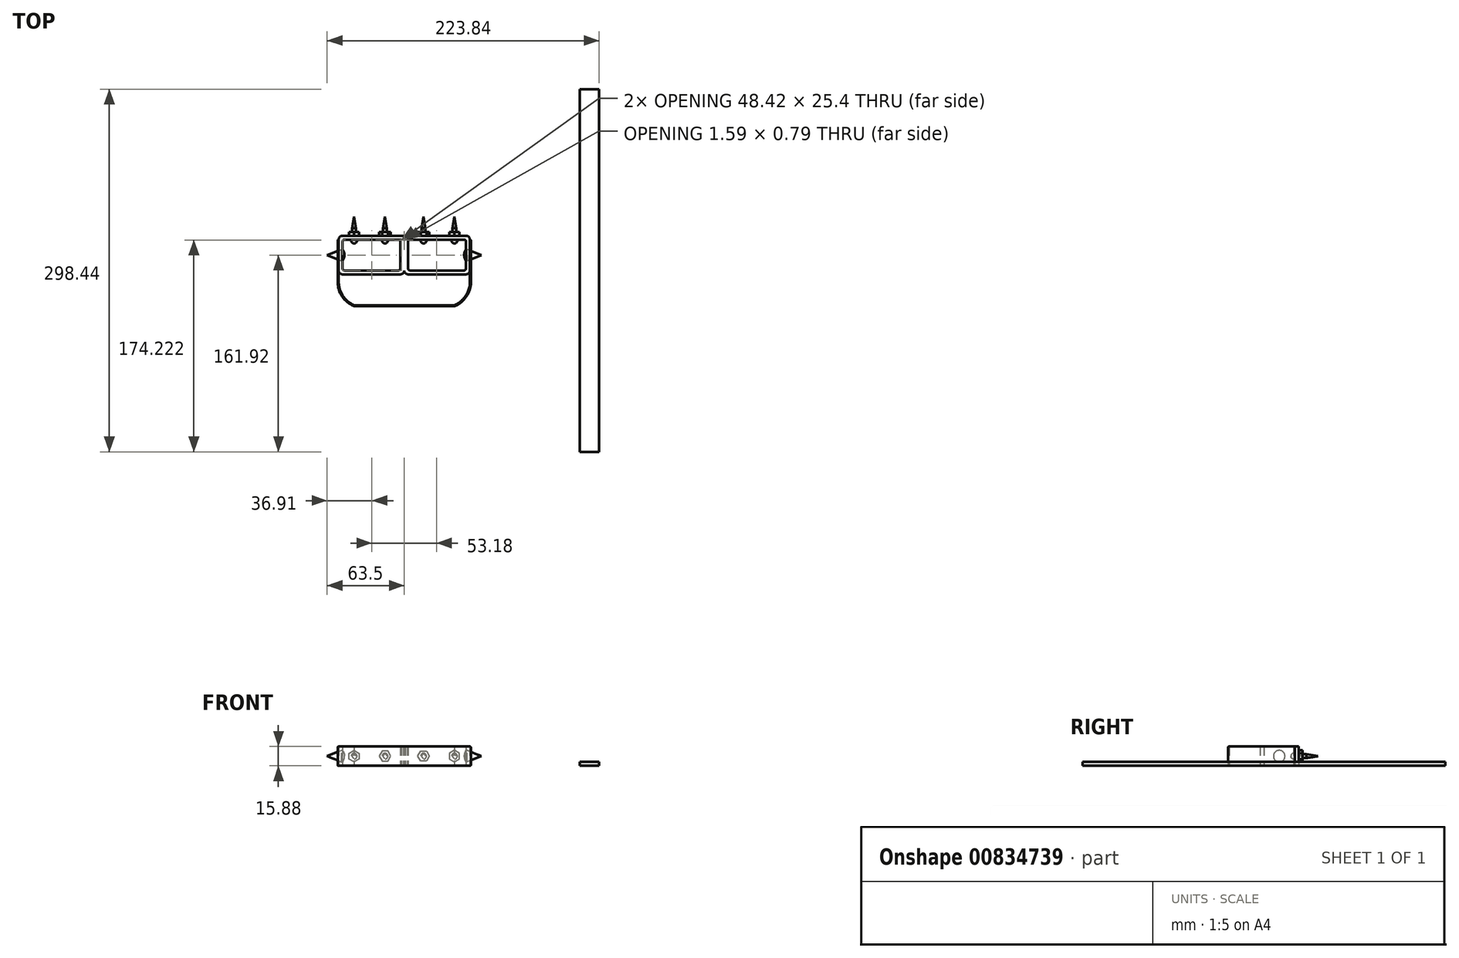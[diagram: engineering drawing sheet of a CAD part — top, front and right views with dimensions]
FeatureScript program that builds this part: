
annotation { "Feature Type Name" : "Feature", "Feature Type Description" : "" }
export const myFeature = defineFeature(function(context is Context, id is Id, definition is map)
    precondition{}
    {
        {
            var Q0;
            Q0=qCreatedBy(makeId("Top.planeOp"),FACE);
            var sketch = newSketch(context, id + "F0", { "sketchPlane" : qUnion([Q0])});
            skLineSegment(sketch, "E0.bottom", {"start": v(-49.21, 0) * mm, "end": v(-4.76, 0) * mm});
            skLineSegment(sketch, "E0.top", {"start": v(-49.21, 25.4) * mm, "end": v(49.21, 25.4) * mm});
            skLineSegment(sketch, "E0.left", {"start": v(-50.8, 1.59) * mm, "end": v(-50.8, 23.81) * mm});
            skLineSegment(sketch, "E0.right", {"start": v(50.8, 1.59) * mm, "end": v(50.8, 23.81) * mm});
            skLineSegment(sketch, "E1", {"start": v(0, 0) * mm, "end": v(0, 24.6) * mm});
            skLineSegment(sketch, "E2", {"start": v(-3.18, 24.6) * mm, "end": v(-3.18, 1.59) * mm});
            skLineSegment(sketch, "E3", {"start": v(3.17, 24.6) * mm, "end": v(3.17, 1.59) * mm});
            skLineSegment(sketch, "E4.bottom", {"start": v(3.18, -3.18) * mm, "end": v(50.8, -3.18) * mm});
            skLineSegment(sketch, "E4.top", {"start": v(-50.8, 28.57) * mm, "end": v(50.8, 28.57) * mm});
            skLineSegment(sketch, "E4.left", {"start": v(-53.98, 0) * mm, "end": v(-53.98, 25.4) * mm});
            skLineSegment(sketch, "E4.right", {"start": v(53.97, 0) * mm, "end": v(53.97, 25.4) * mm});
            skLineSegment(sketch, "E5", {"start": v(0, 0) * mm, "end": v(0, 0) * mm});
            skLineSegment(sketch, "E6.trimOffspring", {"start": v(4.76, 0) * mm, "end": v(49.21, 0) * mm});
            skPoint(sketch, "E7.visualSharp", {"position": v(-50.8, 25.4) * mm});
            skArc(sketch, "E7.filletArc", {"start": v(-49.21, 25.4) * mm, "mid": v(-50.34, 24.94) * mm, "end": v(-50.8, 23.81) * mm});
            skPoint(sketch, "E8.visualSharp", {"position": v(-53.98, 28.57) * mm});
            skArc(sketch, "E8.filletArc", {"start": v(-50.8, 28.57) * mm, "mid": v(-53.05, 27.65) * mm, "end": v(-53.98, 25.4) * mm});
            skPoint(sketch, "E9.visualSharp", {"position": v(-50.8, 0) * mm});
            skArc(sketch, "E9.filletArc", {"start": v(-50.8, 1.59) * mm, "mid": v(-50.34, 0.46) * mm, "end": v(-49.21, 0) * mm});
            skPoint(sketch, "E10.visualSharp", {"position": v(-3.17, 0) * mm});
            skArc(sketch, "E10.filletArc", {"start": v(-4.76, 0) * mm, "mid": v(-3.64, 0.46) * mm, "end": v(-3.18, 1.59) * mm});
            skPoint(sketch, "E11.visualSharp", {"position": v(3.17, 0) * mm});
            skArc(sketch, "E11.filletArc", {"start": v(3.17, 1.59) * mm, "mid": v(3.64, 0.46) * mm, "end": v(4.76, 0) * mm});
            skPoint(sketch, "E12.visualSharp", {"position": v(50.8, 0) * mm});
            skArc(sketch, "E12.filletArc", {"start": v(49.21, 0) * mm, "mid": v(50.34, 0.46) * mm, "end": v(50.8, 1.59) * mm});
            skPoint(sketch, "E13.visualSharp", {"position": v(50.8, 25.4) * mm});
            skArc(sketch, "E13.filletArc", {"start": v(50.8, 23.81) * mm, "mid": v(50.34, 24.94) * mm, "end": v(49.21, 25.4) * mm});
            skPoint(sketch, "E14.visualSharp", {"position": v(53.97, 28.57) * mm});
            skArc(sketch, "E14.filletArc", {"start": v(53.97, 25.4) * mm, "mid": v(53.05, 27.65) * mm, "end": v(50.8, 28.58) * mm});
            skPoint(sketch, "E15.visualSharp", {"position": v(53.97, -3.18) * mm});
            skArc(sketch, "E15.filletArc", {"start": v(50.8, -3.18) * mm, "mid": v(53.05, -2.25) * mm, "end": v(53.97, 0) * mm});
            skPoint(sketch, "E16.newPointB", {"position": v(0, -3.18) * mm});
            skArc(sketch, "E16.filletArc", {"start": v(0, 0) * mm, "mid": v(0.93, -2.25) * mm, "end": v(3.18, -3.17) * mm});
            skLineSegment(sketch, "E17", {"start": v(0, -3.18) * mm, "end": v(0, -3.18) * mm});
            skLineSegment(sketch, "E18", {"start": v(-3.18, -3.18) * mm, "end": v(-50.8, -3.18) * mm});
            skArc(sketch, "E19.filletArc", {"start": v(-3.18, -3.17) * mm, "mid": v(-0.93, -2.25) * mm, "end": v(0, 0) * mm});
            skPoint(sketch, "E20.visualSharp", {"position": v(-53.98, -3.18) * mm});
            skArc(sketch, "E20.filletArc", {"start": v(-53.97, 0) * mm, "mid": v(-53.05, -2.25) * mm, "end": v(-50.8, -3.18) * mm});
            skLineSegment(sketch, "E21", {"start": v(-2.38, 25.4) * mm, "end": v(-0.8, 25.4) * mm});
            skLineSegment(sketch, "E22", {"start": v(0.8, 25.4) * mm, "end": v(2.38, 25.4) * mm});
            skPoint(sketch, "E23.visualSharp", {"position": v(3.17, 25.4) * mm});
            skArc(sketch, "E23.filletArc", {"start": v(3.17, 24.6) * mm, "mid": v(2.94, 25.17) * mm, "end": v(2.38, 25.4) * mm});
            skPoint(sketch, "E24.visualSharp", {"position": v(0, 25.4) * mm});
            skArc(sketch, "E24.filletArc", {"start": v(0.8, 25.4) * mm, "mid": v(0.23, 25.17) * mm, "end": v(0, 24.6) * mm});
            skLineSegment(sketch, "E25", {"start": v(0, 24.6) * mm, "end": v(0, 24.6) * mm});
            skArc(sketch, "E26.filletArc", {"start": v(0, 24.6) * mm, "mid": v(-0.23, 25.17) * mm, "end": v(-0.8, 25.4) * mm});
            skPoint(sketch, "E27.visualSharp", {"position": v(-3.18, 25.4) * mm});
            skArc(sketch, "E27.filletArc", {"start": v(-2.38, 25.4) * mm, "mid": v(-2.94, 25.17) * mm, "end": v(-3.18, 24.6) * mm});
            skLineSegment(sketch, "E28.bottom", {"start": v(-53.97, -3.18) * mm, "end": v(53.97, -3.18) * mm, "construction": true});
            skLineSegment(sketch, "E28.top", {"start": v(-41.27, -28.58) * mm, "end": v(41.28, -28.58) * mm});
            skLineSegment(sketch, "E28.left", {"start": v(-53.98, -3.18) * mm, "end": v(-53.98, -9.53) * mm});
            skLineSegment(sketch, "E28.right", {"start": v(53.97, -3.18) * mm, "end": v(53.97, -9.53) * mm});
            skLineSegment(sketch, "E29", {"start": v(-53.98, 0) * mm, "end": v(-53.98, -3.18) * mm});
            skLineSegment(sketch, "E30", {"start": v(53.97, 0) * mm, "end": v(53.97, -3.18) * mm});
            skPoint(sketch, "E31", {"position": v(-53.97, -9.53) * mm});
            skPoint(sketch, "E32", {"position": v(-41.27, -28.58) * mm});
            skPoint(sketch, "E33", {"position": v(41.28, -28.58) * mm});
            skPoint(sketch, "E34", {"position": v(53.98, -9.53) * mm});
            skArc(sketch, "E35", {"start": v(-53.97, -9.53) * mm, "mid": v(-50.5, -20.97) * mm, "end": v(-41.27, -28.58) * mm});
            skArc(sketch, "E36", {"start": v(41.28, -28.58) * mm, "mid": v(50.5, -20.97) * mm, "end": v(53.98, -9.53) * mm});
            skPoint(sketch, "E37.orphan", {"position": v(53.97, -28.58) * mm});
            skPoint(sketch, "E38.orphan", {"position": v(-53.97, -28.58) * mm});
            skLineSegment(sketch, "E39", {"start": v(54.77, 25.4) * mm, "end": v(54.77, -9.53) * mm});
            skLineSegment(sketch, "E40", {"start": v(-54.77, 25.4) * mm, "end": v(-54.77, -9.53) * mm});
            skLineSegment(sketch, "E41", {"start": v(-41.27, -29.37) * mm, "end": v(41.27, -29.37) * mm});
            skLineSegment(sketch, "E42", {"start": v(-54.77, 25.4) * mm, "end": v(-53.98, 25.4) * mm});
            skLineSegment(sketch, "E43", {"start": v(54.77, 25.4) * mm, "end": v(53.97, 25.4) * mm});
            skArc(sketch, "E44", {"start": v(41.27, -29.37) * mm, "mid": v(51.08, -21.52) * mm, "end": v(54.77, -9.53) * mm});
            skArc(sketch, "E45", {"start": v(-54.77, -9.53) * mm, "mid": v(-51.08, -21.52) * mm, "end": v(-41.27, -29.37) * mm});
            skSolve(sketch);
        }
        {
            var Q0;
            Q0=makeQuery(id+"F0.imprint","IMPRINT",FACE,{"disambiguationData":[TD([[makeQuery(id+"F0.imprint","IMPRINT",EDGE,{"derivedFrom":sQuery(id+"F0.wireOp",EDGE,"E0.bottom")}),-1.0]])]});
            extrude(context, id + "F1", {"entities" : qUnion([Q0]), "depth" : 15.88 * mm, "offsetDistance" : 25.4 * mm});
        }
        {
            var Q0;
            Q0=sQuery(id+"F0.wireOp",EDGE,"E1");
            extrude(context, id + "F2", {"bodyType" : ToolBodyType.SURFACE, "surfaceEntities" : qUnion([Q0]), "depth" : 15.88 * mm, "offsetDistance" : 25.4 * mm});
        }
        {
            var Q0;
            Q0=sQuery(id+"F0.wireOp",EDGE,"E22");
            var Q1;
            Q1=sQuery(id+"F0.wireOp",EDGE,"E21");
            extrude(context, id + "F3", {"bodyType" : ToolBodyType.SURFACE, "surfaceEntities" : qUnion([Q0, Q1]), "depth" : 15.88 * mm, "offsetDistance" : 25.4 * mm});
        }
        {
            var Q0;
            Q0=makeQuery(id+"F0.imprint","IMPRINT",FACE,{"disambiguationData":[TD([[makeQuery(id+"F0.imprint","IMPRINT",EDGE,{"derivedFrom":sQuery(id+"F0.wireOp",EDGE,"E4.bottom")}),-1.0]])]});
            extrude(context, id + "F4", {"entities" : qUnion([Q0]), "depth" : 15.88 * mm, "offsetDistance" : 25.4 * mm});
        }
        {
            var Q0;
            Q0=makeQuery(id+"F0.imprint","IMPRINT",FACE,{"disambiguationData":[TD([[makeQuery(id+"F0.imprint","IMPRINT",EDGE,{"derivedFrom":sQuery(id+"F0.wireOp",EDGE,"E4.left")}),1.0]])]});
            extrude(context, id + "F5", {"entities" : qUnion([Q0]), "depth" : 15.88 * mm, "offsetDistance" : 25.4 * mm});
        }
        {
            var Q0;
            Q0=makeQuery(id+"F5.opExtrude","SWEPT_FACE",FACE,{"disambiguationData":[OSD([sQuery(id+"F0.wireOp",EDGE,"E41")])]});
            var Q1;
            Q1=makeQuery(id+"F5.opExtrude","SWEPT_FACE",FACE,{"disambiguationData":[OSD([sQuery(id+"F0.wireOp",EDGE,"E45")])]});
            var Q2;
            Q2=makeQuery(id+"F5.opExtrude","SWEPT_FACE",FACE,{"disambiguationData":[OSD([sQuery(id+"F0.wireOp",EDGE,"E40")])]});
            var Q3;
            Q3=makeQuery(id+"F5.opExtrude","SWEPT_FACE",FACE,{"disambiguationData":[OSD([sQuery(id+"F0.wireOp",EDGE,"E44")])]});
            var Q4;
            Q4=makeQuery(id+"F5.opExtrude","SWEPT_FACE",FACE,{"disambiguationData":[OSD([sQuery(id+"F0.wireOp",EDGE,"E39")])]});
            fillet(context, id + "F6", {"entities" : qUnion([Q0, Q1, Q2, Q3, Q4]), "radius" : 0.8 * mm, "tangentPropagation" : true, "allowEdgeOverflow" : false});
        }
        {
            var Q0;
            Q0=qCreatedBy(makeId("Right.planeOp"),FACE);
            var sketch = newSketch(context, id + "F7", { "sketchPlane" : qUnion([Q0])});
            skCircle(sketch, "E46", {"center": v(12.7, 7.95) * mm, "radius": 4.76 * mm});
            skSolve(sketch);
        }
        {
            var Q0;
            Q0 = qSketchRegion(id + "F7", true);
            extrude(context, id + "F8", {"entities" : qUnion([Q0]), "depth" : 63.5 * mm, "offsetDistance" : 25.4 * mm, "hasSecondDirection" : true, "secondDirectionOppositeDirection" : false, "secondDirectionDepth" : 49.23 * mm});
        }
        {
            var Q0;
            Q0 = qSketchRegion(id + "F7", true);
            extrude(context, id + "F9", {"entities" : qUnion([Q0]), "oppositeDirection" : true, "depth" : 63.5 * mm, "offsetDistance" : 25.4 * mm, "hasSecondDirection" : true, "secondDirectionOppositeDirection" : true, "secondDirectionDepth" : 49.23 * mm});
        }
        {
            var Q0;
            Q0=makeQuery(id+"F9.opExtrude","CAP_EDGE",EDGE,{"disambiguationData":[OSD([sQuery(id+"F7.wireOp",EDGE,"E46")])],"isStart":false});
            chamfer(context, id + "F10", {"entities" : qUnion([Q0]), "chamferType" : ChamferType.TWO_OFFSETS, "width1" : 11.9 * mm, "oppositeDirection" : false, "width2" : 4.76 * mm, "tangentPropagation" : true});
        }
        {
            var Q0;
            Q0=makeQuery(id+"F8.opExtrude","CAP_EDGE",EDGE,{"disambiguationData":[OSD([sQuery(id+"F7.wireOp",EDGE,"E46")])],"isStart":false});
            chamfer(context, id + "F11", {"entities" : qUnion([Q0]), "chamferType" : ChamferType.TWO_OFFSETS, "width1" : 4.76 * mm, "oppositeDirection" : false, "width2" : 11.9 * mm, "tangentPropagation" : true});
        }
        {
            var Q0;
            Q0=makeQuery(id+"F8.opExtrude","CAP_EDGE",EDGE,{"disambiguationData":[OSD([sQuery(id+"F7.wireOp",EDGE,"E46")])],"isStart":true});
            chamfer(context, id + "F12", {"entities" : qUnion([Q0]), "chamferType" : ChamferType.TWO_OFFSETS, "width1" : 1.59 * mm, "oppositeDirection" : false, "width2" : 2.54 * mm, "tangentPropagation" : true});
        }
        {
            var Q0;
            Q0=makeQuery(id+"F9.opExtrude","CAP_EDGE",EDGE,{"disambiguationData":[OSD([sQuery(id+"F7.wireOp",EDGE,"E46")])],"isStart":true});
            chamfer(context, id + "F13", {"entities" : qUnion([Q0]), "chamferType" : ChamferType.TWO_OFFSETS, "width1" : 2.54 * mm, "oppositeDirection" : false, "width2" : 1.59 * mm, "tangentPropagation" : true});
        }
        {
            var Q0;
            {var subQ0=sQuery(id+"F7.wireOp",EDGE,"E46");Q0=makeQuery(id+"F13.opChamfer","BLEND_EDGE",EDGE,{"blendedFrom":[makeQuery(id+"F9.opExtrude","CAP_EDGE",EDGE,{"disambiguationData":[OSD([subQ0])],"isStart":true}),makeQuery(id+"F9.opExtrude","CAP_FACE",FACE,{"disambiguationData":[OSD([subQ0])],"isStart":true})],"blendedInto":[makeQuery(id+"F9.opExtrude","CAP_FACE",FACE,{"disambiguationData":[OSD([subQ0])],"isStart":true})]});}
            var Q1;
            {var subQ0=sQuery(id+"F7.wireOp",EDGE,"E46");Q1=makeQuery(id+"F12.opChamfer","BLEND_EDGE",EDGE,{"blendedFrom":[makeQuery(id+"F8.opExtrude","CAP_EDGE",EDGE,{"disambiguationData":[OSD([subQ0])],"isStart":true}),makeQuery(id+"F8.opExtrude","CAP_FACE",FACE,{"disambiguationData":[OSD([subQ0])],"isStart":true})],"blendedInto":[makeQuery(id+"F8.opExtrude","CAP_FACE",FACE,{"disambiguationData":[OSD([subQ0])],"isStart":true})]});}
            fillet(context, id + "F14", {"entities" : qUnion([Q0, Q1]), "radius" : 7.75 * mm, "tangentPropagation" : true, "allowEdgeOverflow" : false});
        }
        {
            var Q0;
            Q0=qCreatedBy(makeId("Front.planeOp"),FACE);
            var sketch = newSketch(context, id + "F15", { "sketchPlane" : qUnion([Q0])});
            skLineSegment(sketch, "E47", {"start": v(0, -22.17) * mm, "end": v(0, 47.33) * mm, "construction": true});
            skLineSegment(sketch, "E48", {"start": v(0, 7.95) * mm, "end": v(-82.65, 7.95) * mm, "construction": true});
            skCircle(sketch, "E49", {"center": v(-15.88, 7.95) * mm, "radius": 4.76 * mm, "construction": true});
            skCircle(sketch, "E50", {"center": v(-41.28, 7.95) * mm, "radius": 4.76 * mm, "construction": true});
            skLineSegment(sketch, "E51", {"start": v(-13.5, 3.83) * mm, "end": v(-11.11, 7.95) * mm});
            skLineSegment(sketch, "E52", {"start": v(-11.11, 7.95) * mm, "end": v(-13.5, 12.07) * mm});
            skLineSegment(sketch, "E53", {"start": v(-13.5, 12.07) * mm, "end": v(-18.26, 12.07) * mm});
            skLineSegment(sketch, "E54", {"start": v(-18.26, 12.07) * mm, "end": v(-20.64, 7.95) * mm});
            skLineSegment(sketch, "E55", {"start": v(-20.64, 7.95) * mm, "end": v(-18.26, 3.83) * mm});
            skLineSegment(sketch, "E56", {"start": v(-18.26, 3.83) * mm, "end": v(-13.5, 3.83) * mm});
            skLineSegment(sketch, "E57", {"start": v(-37.15, 10.33) * mm, "end": v(-37.15, 5.57) * mm});
            skLineSegment(sketch, "E58", {"start": v(-37.15, 5.57) * mm, "end": v(-41.28, 3.19) * mm});
            skLineSegment(sketch, "E59", {"start": v(-41.28, 3.19) * mm, "end": v(-45.4, 5.57) * mm});
            skLineSegment(sketch, "E60", {"start": v(-45.4, 5.57) * mm, "end": v(-45.4, 10.33) * mm});
            skLineSegment(sketch, "E61", {"start": v(-45.4, 10.33) * mm, "end": v(-41.28, 12.71) * mm});
            skLineSegment(sketch, "E62", {"start": v(-41.28, 12.71) * mm, "end": v(-37.15, 10.33) * mm});
            skSolve(sketch);
        }
        {
            var Q0;
            Q0 = qSketchRegion(id + "F15", true);
            extrude(context, id + "F16", {"entities" : qUnion([Q0]), "oppositeDirection" : true, "depth" : 31.75 * mm, "offsetDistance" : 25.4 * mm, "hasSecondDirection" : true, "secondDirectionOppositeDirection" : true, "secondDirectionDepth" : 28.57 * mm});
        }
        {
            var Q0;
            Q0=qCreatedBy(makeId("Front.planeOp"),FACE);
            var sketch = newSketch(context, id + "F17", { "sketchPlane" : qUnion([Q0])});
            skCircle(sketch, "E63", {"center": v(-15.88, 7.95) * mm, "radius": 1.59 * mm});
            skCircle(sketch, "E64", {"center": v(-41.28, 7.95) * mm, "radius": 1.59 * mm});
            skSolve(sketch);
        }
        {
            var Q0;
            Q0 = qSketchRegion(id + "F17", true);
            extrude(context, id + "F18", {"entities" : qUnion([Q0]), "oppositeDirection" : true, "depth" : 44.45 * mm, "offsetDistance" : 25.4 * mm, "hasSecondDirection" : true, "secondDirectionOppositeDirection" : true, "secondDirectionDepth" : 31.75 * mm});
        }
        {
            var Q0;
            Q0=makeQuery(id+"F18.opExtrude","CAP_EDGE",EDGE,{"disambiguationData":[OSD([sQuery(id+"F17.wireOp",EDGE,"E63")])],"isStart":false});
            var Q1;
            Q1=makeQuery(id+"F18.opExtrude","CAP_EDGE",EDGE,{"disambiguationData":[OSD([sQuery(id+"F17.wireOp",EDGE,"E64")])],"isStart":false});
            chamfer(context, id + "F19", {"entities" : qUnion([Q0, Q1]), "chamferType" : ChamferType.TWO_OFFSETS, "width1" : 9.52 * mm, "oppositeDirection" : false, "width2" : 1.59 * mm, "tangentPropagation" : true});
        }
        {
            var Q0;
            Q0=qCreatedBy(makeId("Front.planeOp"),FACE);
            var sketch = newSketch(context, id + "F20", { "sketchPlane" : qUnion([Q0])});
            skCircle(sketch, "E65", {"center": v(-15.88, 7.95) * mm, "radius": 2.38 * mm});
            skCircle(sketch, "E66", {"center": v(-41.28, 7.95) * mm, "radius": 2.38 * mm});
            skSolve(sketch);
        }
        {
            var Q0;
            Q0 = qSketchRegion(id + "F20", true);
            extrude(context, id + "F21", {"entities" : qUnion([Q0]), "oppositeDirection" : true, "depth" : 25.4 * mm, "offsetDistance" : 25.4 * mm, "hasSecondDirection" : true, "secondDirectionOppositeDirection" : true, "secondDirectionDepth" : 22.22 * mm});
        }
        {
            var Q0;
            Q0=makeQuery(id+"F21.opExtrude","CAP_EDGE",EDGE,{"disambiguationData":[OSD([sQuery(id+"F20.wireOp",EDGE,"E65")])],"isStart":true});
            var Q1;
            Q1=makeQuery(id+"F21.opExtrude","CAP_EDGE",EDGE,{"disambiguationData":[OSD([sQuery(id+"F20.wireOp",EDGE,"E66")])],"isStart":true});
            fillet(context, id + "F22", {"entities" : qUnion([Q0, Q1]), "radius" : 2.38 * mm, "tangentPropagation" : true, "allowEdgeOverflow" : false});
        }
        {
            var Q0;
            Q0=makeQuery(id+"F21.opExtrude","SWEPT_BODY",BODY,{"disambiguationData":[OSD([sQuery(id+"F20.wireOp",EDGE,"E65")])]});
            var Q1;
            Q1=makeQuery(id+"F18.opExtrude","SWEPT_BODY",BODY,{"disambiguationData":[OSD([sQuery(id+"F17.wireOp",EDGE,"E64")])]});
            var Q2;
            Q2=makeQuery(id+"F21.opExtrude","SWEPT_BODY",BODY,{"disambiguationData":[OSD([sQuery(id+"F20.wireOp",EDGE,"E66")])]});
            var Q3;
            Q3=makeQuery(id+"F18.opExtrude","SWEPT_BODY",BODY,{"disambiguationData":[OSD([sQuery(id+"F17.wireOp",EDGE,"E63")])]});
            var Q4;
            Q4=makeQuery(id+"F16.opExtrude","SWEPT_BODY",BODY,{"disambiguationData":[OSD([sQuery(id+"F15.wireOp",EDGE,"E57"),sQuery(id+"F15.wireOp",EDGE,"E58"),sQuery(id+"F15.wireOp",EDGE,"E59"),sQuery(id+"F15.wireOp",EDGE,"E60"),sQuery(id+"F15.wireOp",EDGE,"E61"),sQuery(id+"F15.wireOp",EDGE,"E62")])]});
            var Q5;
            Q5=makeQuery(id+"F16.opExtrude","SWEPT_BODY",BODY,{"disambiguationData":[OSD([sQuery(id+"F15.wireOp",EDGE,"E51"),sQuery(id+"F15.wireOp",EDGE,"E52"),sQuery(id+"F15.wireOp",EDGE,"E53"),sQuery(id+"F15.wireOp",EDGE,"E54"),sQuery(id+"F15.wireOp",EDGE,"E55"),sQuery(id+"F15.wireOp",EDGE,"E56")])]});
            var Q6;
            Q6=qCreatedBy(makeId("Right.planeOp"),FACE);
            mirror(context, id + "F23", {"entities" : qUnion([Q0, Q1, Q2, Q3, Q4, Q5]), "mirrorPlane" : qUnion([Q6])});
        }
        {
            var Q0;
            Q0=qCreatedBy(makeId("Top.planeOp"),FACE);
            var sketch = newSketch(context, id + "F24", { "sketchPlane" : qUnion([Q0])});
            skLineSegment(sketch, "E67.bottom", {"start": v(160.34, -149.22) * mm, "end": v(144.46, -149.22) * mm});
            skLineSegment(sketch, "E67.top", {"start": v(160.34, 149.23) * mm, "end": v(144.46, 149.23) * mm});
            skLineSegment(sketch, "E67.left", {"start": v(160.34, -149.22) * mm, "end": v(160.34, 149.23) * mm});
            skLineSegment(sketch, "E67.right", {"start": v(144.46, -149.22) * mm, "end": v(144.46, 149.23) * mm});
            skPoint(sketch, "E67.middle", {"position": v(152.4, 0) * mm});
            skLineSegment(sketch, "E68", {"start": v(144.46, 123.83) * mm, "end": v(160.34, 123.83) * mm});
            skLineSegment(sketch, "E69", {"start": v(144.46, 76.2) * mm, "end": v(160.34, 76.2) * mm});
            skLineSegment(sketch, "E70", {"start": v(144.46, 50.8) * mm, "end": v(160.34, 50.8) * mm});
            skLineSegment(sketch, "E71", {"start": v(144.46, -50.8) * mm, "end": v(160.34, -50.8) * mm});
            skLineSegment(sketch, "E72", {"start": v(144.46, -76.2) * mm, "end": v(160.34, -76.2) * mm});
            skLineSegment(sketch, "E73", {"start": v(144.46, -123.82) * mm, "end": v(160.34, -123.82) * mm});
            skSolve(sketch);
        }
        {
            var Q0;
            Q0 = qSketchRegion(id + "F24", true);
            extrude(context, id + "F25", {"entities" : qUnion([Q0]), "depth" : 3.17 * mm, "offsetDistance" : 25.4 * mm});
        }
        {
            var Q0;
            Q0=sQuery(id+"F24.wireOp",EDGE,"E73");
            var Q1;
            Q1=sQuery(id+"F24.wireOp",EDGE,"E72");
            var Q2;
            Q2=sQuery(id+"F24.wireOp",EDGE,"E71");
            var Q3;
            Q3=sQuery(id+"F24.wireOp",EDGE,"E70");
            var Q4;
            Q4=sQuery(id+"F24.wireOp",EDGE,"E69");
            var Q5;
            Q5=sQuery(id+"F24.wireOp",EDGE,"E68");
            extrude(context, id + "F26", {"bodyType" : ToolBodyType.SURFACE, "surfaceEntities" : qUnion([Q0, Q1, Q2, Q3, Q4, Q5]), "depth" : 3.17 * mm, "offsetDistance" : 25.4 * mm});
        }
    });
